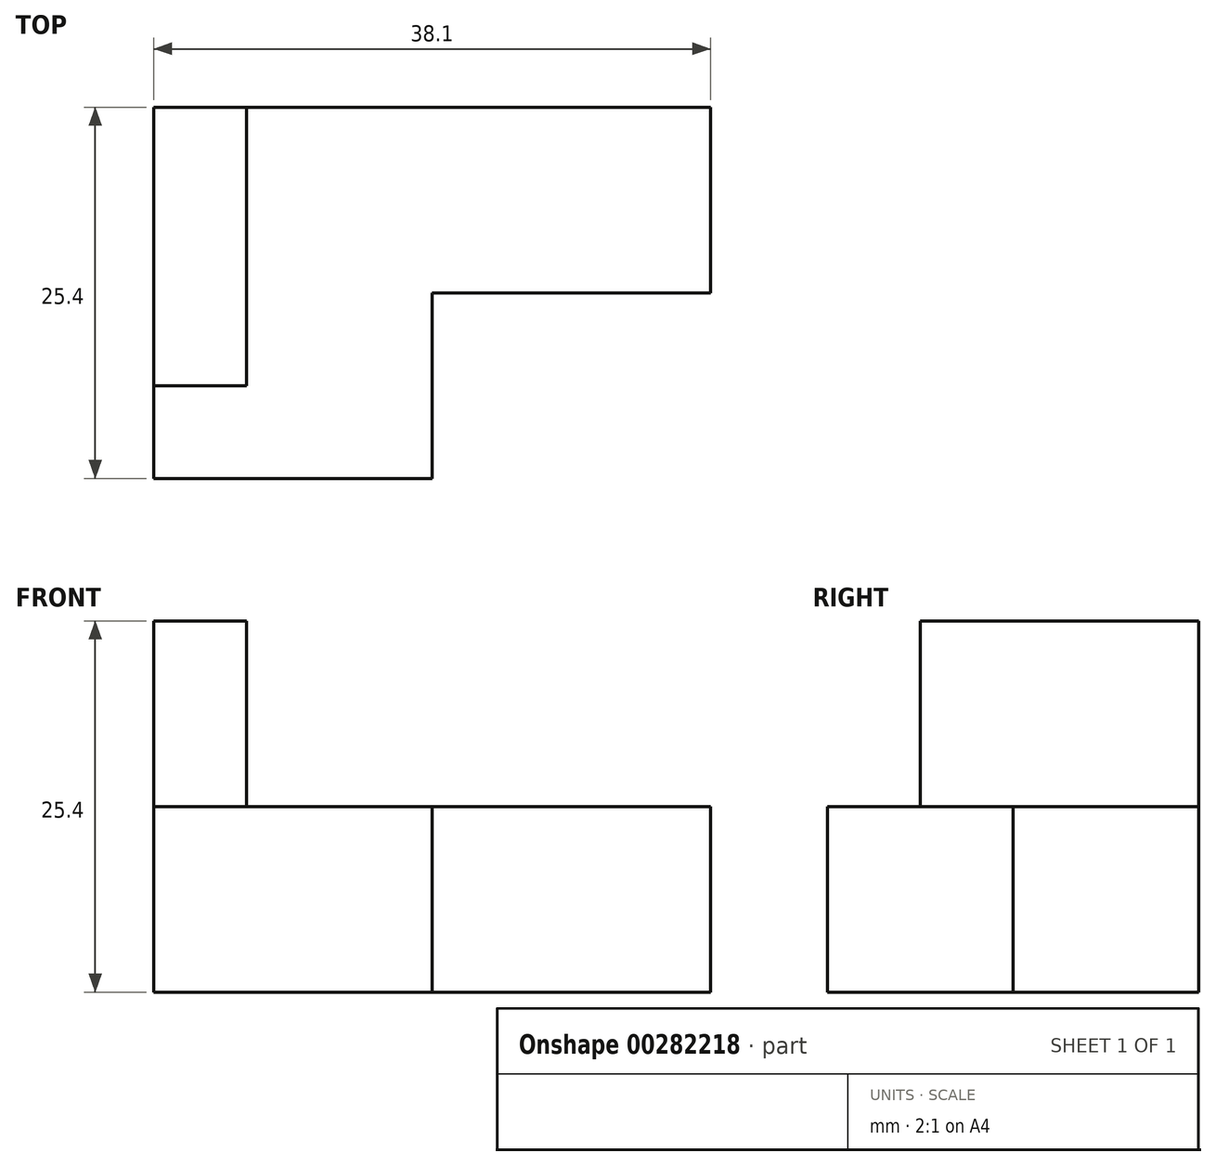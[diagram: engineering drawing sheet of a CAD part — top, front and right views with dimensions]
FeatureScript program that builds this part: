
annotation { "Feature Type Name" : "Feature", "Feature Type Description" : "" }
export const myFeature = defineFeature(function(context is Context, id is Id, definition is map)
    precondition{}
    {
        {
            var Q0;
            Q0=qCreatedBy(makeId("Top.planeOp"),FACE);
            var sketch = newSketch(context, id + "F0", { "sketchPlane" : qUnion([Q0])});
            skLineSegment(sketch, "E0", {"start": v(0, 0) * mm, "end": v(0, 25.4) * mm});
            skLineSegment(sketch, "E1", {"start": v(0, 25.4) * mm, "end": v(38.1, 25.4) * mm});
            skLineSegment(sketch, "E2", {"start": v(38.1, 25.4) * mm, "end": v(38.1, 12.7) * mm});
            skLineSegment(sketch, "E3", {"start": v(38.1, 12.7) * mm, "end": v(19.05, 12.7) * mm});
            skLineSegment(sketch, "E4", {"start": v(19.05, 12.7) * mm, "end": v(19.05, 0) * mm});
            skLineSegment(sketch, "E5", {"start": v(19.05, 0) * mm, "end": v(0, 0) * mm});
            skSolve(sketch);
        }
        {
            var Q0;
            Q0=makeQuery(id+"F0.imprint","IMPRINT",FACE,{"disambiguationData":[TD([[makeQuery(id+"F0.imprint","IMPRINT",EDGE,{"derivedFrom":sQuery(id+"F0.wireOp",EDGE,"E0")}),-1.0]])]});
            extrude(context, id + "F1", {"entities" : qUnion([Q0]), "oppositeDirection" : true, "depth" : 12.7 * mm});
        }
        {
            var Q0;
            Q0=makeQuery(id+"F1.opExtrude","CAP_FACE",FACE,{"disambiguationData":[OSD([sQuery(id+"F0.wireOp",EDGE,"E0"),sQuery(id+"F0.wireOp",EDGE,"E1"),sQuery(id+"F0.wireOp",EDGE,"E2"),sQuery(id+"F0.wireOp",EDGE,"E3"),sQuery(id+"F0.wireOp",EDGE,"E4"),sQuery(id+"F0.wireOp",EDGE,"E5")])],"isStart":true});
            var sketch = newSketch(context, id + "F2", { "sketchPlane" : qUnion([Q0])});
            skLineSegment(sketch, "E6.bottom", {"start": v(0, 25.4) * mm, "end": v(6.35, 25.4) * mm});
            skLineSegment(sketch, "E6.top", {"start": v(0, 6.35) * mm, "end": v(6.35, 6.35) * mm});
            skLineSegment(sketch, "E6.left", {"start": v(0, 25.4) * mm, "end": v(0, 6.35) * mm});
            skLineSegment(sketch, "E6.right", {"start": v(6.35, 25.4) * mm, "end": v(6.35, 6.35) * mm});
            skSolve(sketch);
        }
        {
            var Q0;
            Q0=makeQuery(id+"F2.imprint","IMPRINT",FACE,{"disambiguationData":[TD([[makeQuery(id+"F2.imprint","IMPRINT",EDGE,{"derivedFrom":sQuery(id+"F2.wireOp",EDGE,"E6.bottom")}),-1.0]])]});
            extrude(context, id + "F3", {"entities" : qUnion([Q0]), "operationType" : NewBodyOperationType.ADD, "depth" : 12.7 * mm});
        }
    });
